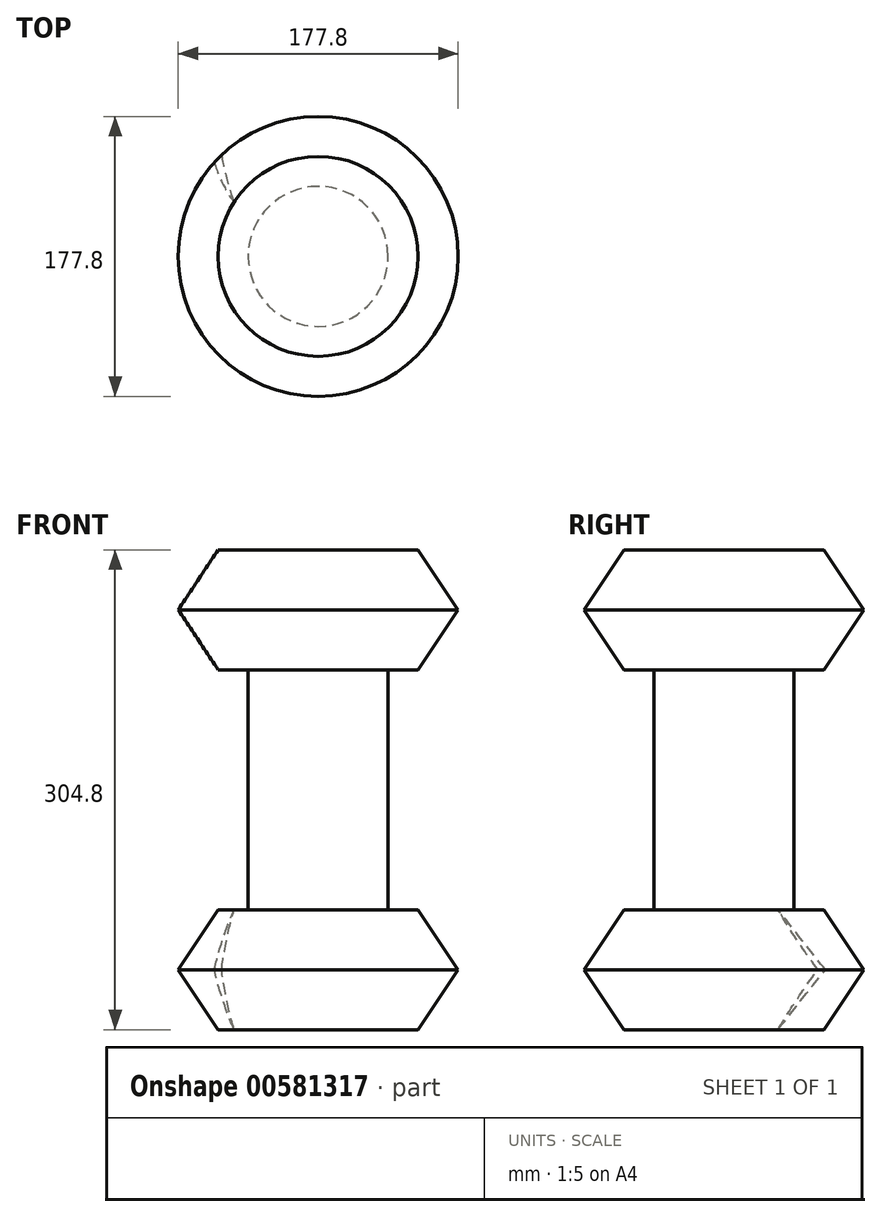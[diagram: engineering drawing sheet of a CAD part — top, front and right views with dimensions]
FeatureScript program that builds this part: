
annotation { "Feature Type Name" : "Feature", "Feature Type Description" : "" }
export const myFeature = defineFeature(function(context is Context, id is Id, definition is map)
    precondition{}
    {
        {
            var Q0;
            Q0=qCreatedBy(makeId("Front.planeOp"),FACE);
            var sketch = newSketch(context, id + "F0", { "sketchPlane" : qUnion([Q0])});
            skLineSegment(sketch, "E0", {"start": v(0, 0) * mm, "end": v(0, 152.4) * mm});
            skLineSegment(sketch, "E1", {"start": v(0, 152.4) * mm, "end": v(-63.5, 152.4) * mm});
            skLineSegment(sketch, "E2", {"start": v(-63.5, 152.4) * mm, "end": v(-88.9, 114.3) * mm});
            skLineSegment(sketch, "E3", {"start": v(-88.9, 114.3) * mm, "end": v(-63.5, 76.2) * mm});
            skLineSegment(sketch, "E4", {"start": v(-63.5, 76.2) * mm, "end": v(-44.45, 76.2) * mm});
            skLineSegment(sketch, "E5", {"start": v(-44.45, 76.2) * mm, "end": v(-44.45, 0) * mm});
            skLineSegment(sketch, "E6", {"start": v(-44.45, 0) * mm, "end": v(0, 0) * mm, "construction": true});
            skLineSegment(sketch, "E7.MirrorCS", {"start": v(63.5, 76.2) * mm, "end": v(44.45, 76.2) * mm});
            skLineSegment(sketch, "E8.MirrorCS", {"start": v(88.9, 114.3) * mm, "end": v(63.5, 76.2) * mm});
            skLineSegment(sketch, "E9.MirrorCS", {"start": v(63.5, 152.4) * mm, "end": v(88.9, 114.3) * mm});
            skLineSegment(sketch, "E10.MirrorCS", {"start": v(0, 152.4) * mm, "end": v(63.5, 152.4) * mm});
            skLineSegment(sketch, "E11.MirrorCS", {"start": v(0, 0) * mm, "end": v(0, 152.4) * mm, "construction": true});
            skLineSegment(sketch, "E12.MirrorCS", {"start": v(44.45, 0) * mm, "end": v(0, 0) * mm});
            skLineSegment(sketch, "E13.MirrorCS", {"start": v(44.45, 76.2) * mm, "end": v(44.45, 0) * mm});
            skLineSegment(sketch, "E14.MirrorCS", {"start": v(63.5, -76.2) * mm, "end": v(44.45, -76.2) * mm});
            skLineSegment(sketch, "E15.MirrorCS", {"start": v(63.5, -152.4) * mm, "end": v(88.9, -114.3) * mm});
            skLineSegment(sketch, "E16.MirrorCS", {"start": v(0, 0) * mm, "end": v(0, -152.4) * mm, "construction": true});
            skLineSegment(sketch, "E17.MirrorCS", {"start": v(0, -152.4) * mm, "end": v(-63.5, -152.4) * mm});
            skLineSegment(sketch, "E18.MirrorCS", {"start": v(-88.9, -114.3) * mm, "end": v(-63.5, -76.2) * mm});
            skLineSegment(sketch, "E19.MirrorCS", {"start": v(-44.45, -76.2) * mm, "end": v(-44.45, 0) * mm});
            skLineSegment(sketch, "E20.MirrorCS", {"start": v(88.9, -114.3) * mm, "end": v(63.5, -76.2) * mm});
            skLineSegment(sketch, "E21.MirrorCS", {"start": v(0, -152.4) * mm, "end": v(63.5, -152.4) * mm});
            skLineSegment(sketch, "E22.MirrorCS", {"start": v(31.75, 0) * mm, "end": v(0, 0) * mm});
            skLineSegment(sketch, "E23.MirrorCS", {"start": v(44.45, -76.2) * mm, "end": v(44.45, 0) * mm});
            skLineSegment(sketch, "E24.MirrorCS", {"start": v(0, 0) * mm, "end": v(0, -152.4) * mm});
            skLineSegment(sketch, "E25.MirrorCS", {"start": v(-63.5, -152.4) * mm, "end": v(-88.9, -114.3) * mm});
            skLineSegment(sketch, "E26.MirrorCS", {"start": v(-63.5, -76.2) * mm, "end": v(-44.45, -76.2) * mm});
            skSolve(sketch);
        }
        {
            var Q0;
            Q0=makeQuery(id+"F0.imprint","IMPRINT",FACE,{"disambiguationData":[TD([[makeQuery(id+"F0.imprint","IMPRINT",EDGE,{"derivedFrom":sQuery(id+"F0.wireOp",EDGE,"E0")}),1.0]])]});
            var Q1;
            Q1=sQuery(id+"F0.wireOp",EDGE,"E0");
            revolve(context, id + "F1", {"entities" : qUnion([Q0]), "axis" : qUnion([Q1]), "revolveType" : RevolveType.FULL});
        }
        {
            var Q0;
            Q0=makeQuery(id+"F1.opRevolve","SWEPT_FACE",FACE,{"disambiguationData":[OSD([sQuery(id+"F0.wireOp",EDGE,"E17.MirrorCS")])]});
            var sketch = newSketch(context, id + "F2", { "sketchPlane" : qUnion([Q0])});
            skArc(sketch, "E27", {"start": v(-53.42, -34.34) * mm, "mid": v(-68.88, -74.37) * mm, "end": v(-61.99, -116.74) * mm});
            skArc(sketch, "E28", {"start": v(-53.42, -34.34) * mm, "mid": v(-62.89, -75) * mm, "end": v(-61.99, -116.74) * mm});
            skSolve(sketch);
        }
        {
            var Q0;
            Q0 = qSketchRegion(id + "F2", true);
            extrude(context, id + "F3", {"entities" : qUnion([Q0]), "operationType" : NewBodyOperationType.REMOVE, "oppositeDirection" : true, "depth" : 152.4 * mm, "offsetDistance" : 25.4 * mm});
        }
    });
